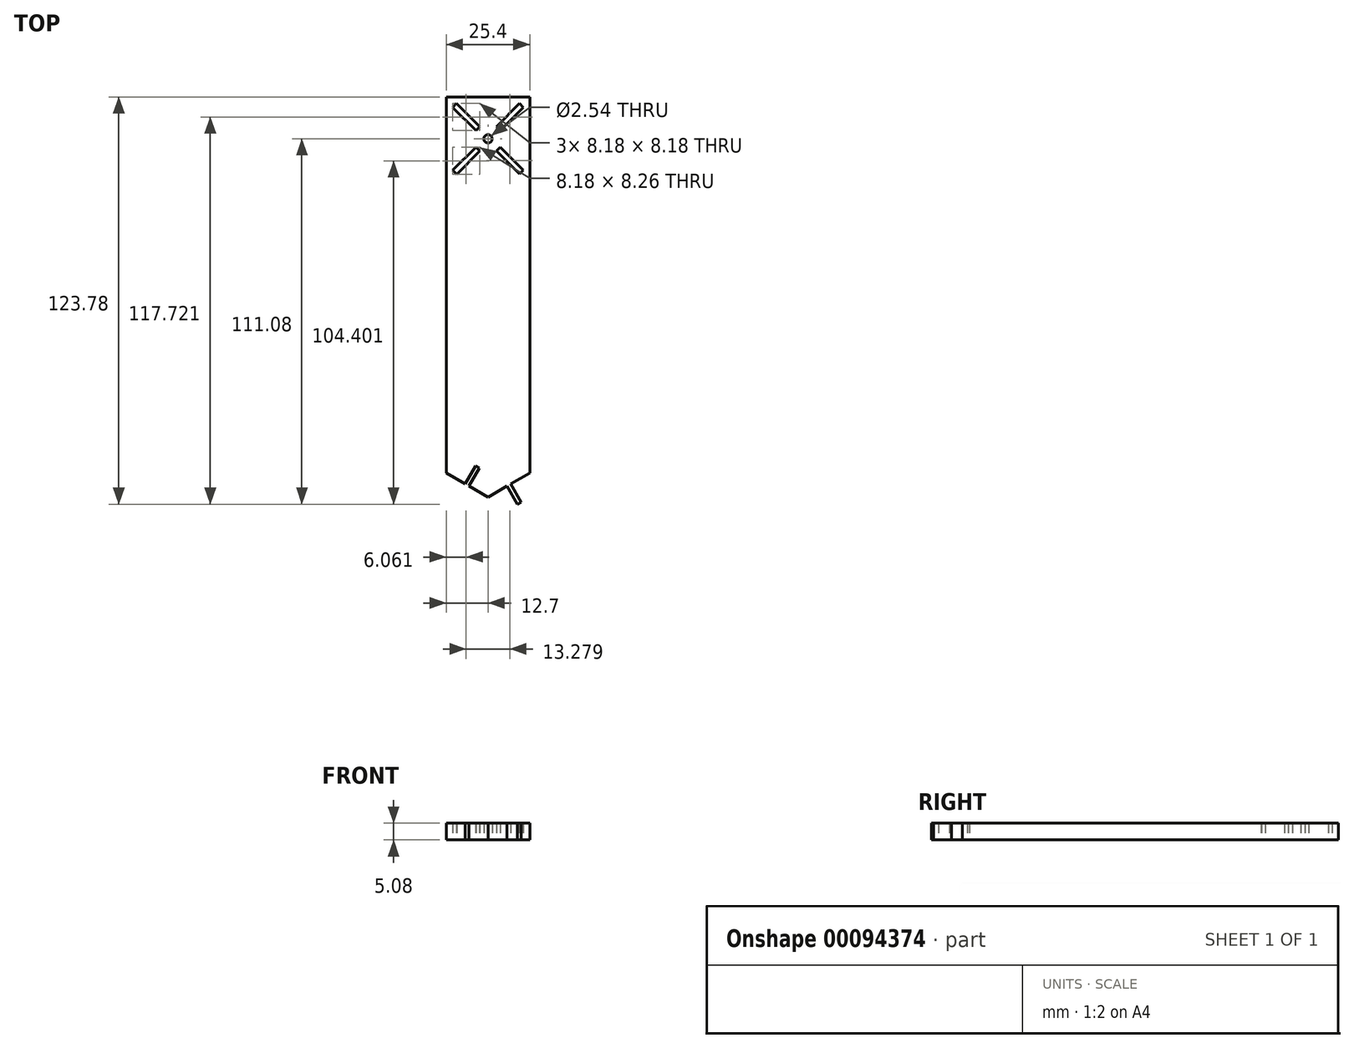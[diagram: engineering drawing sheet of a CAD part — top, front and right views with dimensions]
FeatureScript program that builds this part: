
annotation { "Feature Type Name" : "Feature", "Feature Type Description" : "" }
export const myFeature = defineFeature(function(context is Context, id is Id, definition is map)
    precondition{}
    {
        {
            var Q0;
            Q0=qCreatedBy(makeId("Top.planeOp"),FACE);
            var sketch = newSketch(context, id + "F0", { "sketchPlane" : qUnion([Q0])});
            skLineSegment(sketch, "E0.top", {"start": v(0, 88.9) * mm, "end": v(25.4, 88.9) * mm});
            skLineSegment(sketch, "E0.right", {"start": v(25.4, 0) * mm, "end": v(25.4, 88.9) * mm});
            skLineSegment(sketch, "E1.top", {"start": v(0, 114.3) * mm, "end": v(25.4, 114.3) * mm});
            skLineSegment(sketch, "E1.left", {"start": v(0, 88.9) * mm, "end": v(0, 114.3) * mm});
            skLineSegment(sketch, "E1.right", {"start": v(25.4, 88.9) * mm, "end": v(25.4, 114.3) * mm});
            skCircle(sketch, "E2", {"center": v(12.7, 101.6) * mm, "radius": 1.27 * mm});
            skPoint(sketch, "E2.centerSnap0", {"position": v(12.7, 114.3) * mm});
            skPoint(sketch, "E2.centerSnap1", {"position": v(0, 101.6) * mm});
            skLineSegment(sketch, "E3", {"start": v(15.82, 98.48) * mm, "end": v(15.25, 97.9) * mm});
            skLineSegment(sketch, "E4", {"start": v(15.82, 98.48) * mm, "end": v(16.4, 99.05) * mm});
            skLineSegment(sketch, "E5", {"start": v(16.4, 99.05) * mm, "end": v(23.43, 92.02) * mm});
            skLineSegment(sketch, "E6", {"start": v(23.43, 92.02) * mm, "end": v(22.28, 90.87) * mm});
            skLineSegment(sketch, "E7", {"start": v(15.25, 97.9) * mm, "end": v(22.28, 90.87) * mm});
            skLineSegment(sketch, "E8.MirrorCS", {"start": v(10.15, 105.3) * mm, "end": v(3.12, 112.33) * mm});
            skLineSegment(sketch, "E9.MirrorCS", {"start": v(9, 104.15) * mm, "end": v(1.97, 111.18) * mm});
            skLineSegment(sketch, "E10.MirrorCS", {"start": v(9.58, 104.72) * mm, "end": v(9, 104.15) * mm});
            skLineSegment(sketch, "E11.MirrorCS", {"start": v(9.58, 104.72) * mm, "end": v(10.15, 105.3) * mm});
            skLineSegment(sketch, "E12", {"start": v(1.97, 111.18) * mm, "end": v(3.12, 112.33) * mm});
            skLineSegment(sketch, "E13", {"start": v(15.25, 105.3) * mm, "end": v(16.4, 104.15) * mm});
            skLineSegment(sketch, "E14", {"start": v(10.15, 97.9) * mm, "end": v(9, 99.05) * mm});
            skLineSegment(sketch, "E15", {"start": v(9, 99.05) * mm, "end": v(1.97, 92.02) * mm});
            skLineSegment(sketch, "E16", {"start": v(1.97, 92.02) * mm, "end": v(3.2, 90.79) * mm});
            skLineSegment(sketch, "E17", {"start": v(3.2, 90.79) * mm, "end": v(10.15, 97.9) * mm});
            skLineSegment(sketch, "E18.MirrorCS", {"start": v(16.4, 104.15) * mm, "end": v(23.43, 111.18) * mm});
            skLineSegment(sketch, "E19.MirrorCS", {"start": v(15.25, 105.3) * mm, "end": v(22.28, 112.33) * mm});
            skLineSegment(sketch, "E20", {"start": v(22.28, 112.33) * mm, "end": v(23.43, 111.18) * mm});
            skLineSegment(sketch, "E21", {"start": v(0, 88.9) * mm, "end": v(0, 0) * mm});
            skPoint(sketch, "E22.MirrorCS.end.orphan", {"position": v(3.12, 90.87) * mm});
            skPoint(sketch, "E22.MirrorCS.start.orphan", {"position": v(10.15, 97.9) * mm});
            skPoint(sketch, "E23.start.orphan", {"position": v(12.7, -7.33) * mm});
            skLineSegment(sketch, "E24", {"start": v(12.7, -7.33) * mm, "end": v(6.91, -4) * mm});
            skLineSegment(sketch, "E25", {"start": v(12.7, -7.33) * mm, "end": v(18.5, -3.98) * mm});
            skPoint(sketch, "E26.orphan", {"position": v(25.4, -7.34) * mm});
            skLineSegment(sketch, "E27", {"start": v(9.53, 1.83) * mm, "end": v(8.98, 2.15) * mm});
            skLineSegment(sketch, "E28", {"start": v(9.53, 1.83) * mm, "end": v(10.09, 1.5) * mm});
            skPoint(sketch, "E29.start.orphan", {"position": v(6.35, -3.67) * mm});
            skLineSegment(sketch, "E30", {"start": v(8.98, 2.15) * mm, "end": v(5.8, -3.35) * mm});
            skLineSegment(sketch, "E31", {"start": v(10.09, 1.5) * mm, "end": v(6.91, -4) * mm});
            skLineSegment(sketch, "E32.trimOffspring", {"start": v(5.8, -3.35) * mm, "end": v(0, 0) * mm});
            skLineSegment(sketch, "E33", {"start": v(1.97, 111.18) * mm, "end": v(0, 114.3) * mm});
            skLineSegment(sketch, "E34", {"start": v(22.28, 112.33) * mm, "end": v(25.4, 114.3) * mm});
            skLineSegment(sketch, "E35", {"start": v(23.43, 92.02) * mm, "end": v(25.4, 88.9) * mm});
            skLineSegment(sketch, "E36", {"start": v(3.2, 90.79) * mm, "end": v(0, 88.9) * mm});
            skLineSegment(sketch, "E37", {"start": v(22.22, -9.17) * mm, "end": v(22.77, -8.85) * mm});
            skLineSegment(sketch, "E38", {"start": v(22.22, -9.17) * mm, "end": v(21.68, -9.48) * mm});
            skLineSegment(sketch, "E39", {"start": v(21.68, -9.48) * mm, "end": v(18.5, -3.98) * mm});
            skLineSegment(sketch, "E40", {"start": v(22.77, -8.85) * mm, "end": v(19.6, -3.35) * mm});
            skLineSegment(sketch, "E41.trimOffspring", {"start": v(19.6, -3.35) * mm, "end": v(25.4, 0) * mm});
            skSolve(sketch);
        }
        {
            var Q0;
            Q0 = qSketchRegion(id + "F0", true);
            extrude(context, id + "F1", {"entities" : qUnion([Q0]), "depth" : 5.08 * mm});
        }
    });
